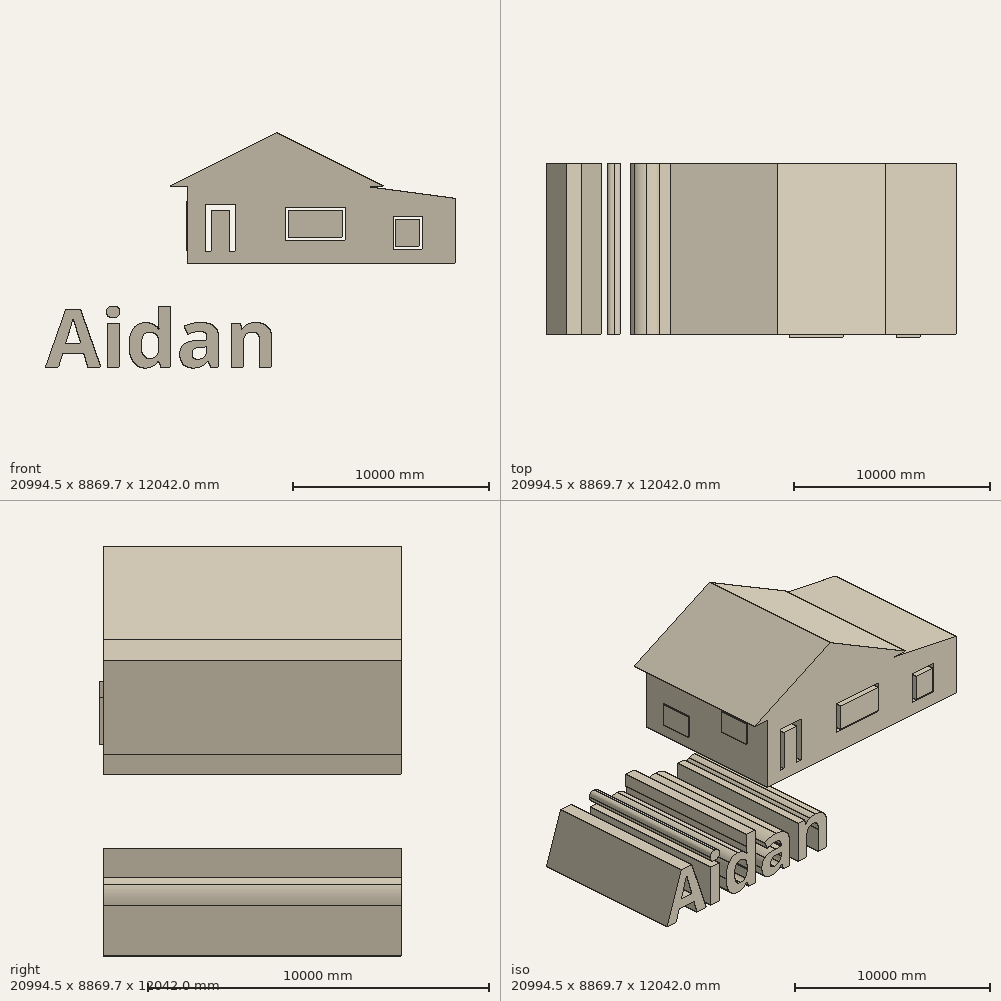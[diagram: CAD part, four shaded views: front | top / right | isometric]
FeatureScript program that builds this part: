
annotation { "Feature Type Name" : "Feature", "Feature Type Description" : "" }
export const myFeature = defineFeature(function(context is Context, id is Id, definition is map)
    precondition{}
    {
        {
            var Q0;
            Q0=qCreatedBy(makeId("Front.planeOp"),FACE);
            var sketch = newSketch(context, id + "F0", { "sketchPlane" : qUnion([Q0])});
            skLineSegment(sketch, "E0", {"start": v(0, 0) * mm, "end": v(-4572, 0) * mm});
            skLineSegment(sketch, "E1", {"start": v(0, 0) * mm, "end": v(4572, 0) * mm});
            skLineSegment(sketch, "E2", {"start": v(0, 0) * mm, "end": v(0, 2286) * mm});
            skLineSegment(sketch, "E3", {"start": v(0, 2286) * mm, "end": v(0, 2743.2) * mm});
            skLineSegment(sketch, "E4", {"start": v(0, 2286) * mm, "end": v(4572, 0) * mm});
            skLineSegment(sketch, "E5", {"start": v(0, 2286) * mm, "end": v(-4572, 0) * mm});
            skLineSegment(sketch, "E6", {"start": v(4572, 0) * mm, "end": v(5486.4, 0) * mm});
            skLineSegment(sketch, "E7", {"start": v(-4572, 0) * mm, "end": v(-5486.4, 0) * mm});
            skLineSegment(sketch, "E8", {"start": v(0, 2743.2) * mm, "end": v(-5486.4, 0) * mm});
            skLineSegment(sketch, "E9", {"start": v(0, 2743.2) * mm, "end": v(5486.4, 0) * mm});
            skLineSegment(sketch, "E10", {"start": v(-4572, 0) * mm, "end": v(-4572, -3352.8) * mm});
            skLineSegment(sketch, "E11", {"start": v(-4572, -3352.8) * mm, "end": v(4572, -3352.8) * mm});
            skLineSegment(sketch, "E12", {"start": v(4572, 0) * mm, "end": v(4572, -3352.8) * mm});
            skLineSegment(sketch, "E13", {"start": v(-4572, -3352.8) * mm, "end": v(-4572, -3962.4) * mm});
            skLineSegment(sketch, "E14.bottom", {"start": v(609.6, -1219.2) * mm, "end": v(3352.8, -1219.2) * mm});
            skLineSegment(sketch, "E14.top", {"start": v(609.6, -2590.8) * mm, "end": v(3352.8, -2590.8) * mm});
            skLineSegment(sketch, "E14.left", {"start": v(609.6, -1219.2) * mm, "end": v(609.6, -2590.8) * mm});
            skLineSegment(sketch, "E14.right", {"start": v(3352.8, -1219.2) * mm, "end": v(3352.8, -2590.8) * mm});
            skLineSegment(sketch, "E15", {"start": v(4572, -3352.8) * mm, "end": v(9144, -3352.8) * mm});
            skLineSegment(sketch, "E16.0", {"start": v(457.2, -1066.8) * mm, "end": v(3505.2, -1066.8) * mm});
            skLineSegment(sketch, "E16.1", {"start": v(457.2, -1066.8) * mm, "end": v(457.2, -2743.2) * mm});
            skLineSegment(sketch, "E16.2", {"start": v(457.2, -2743.2) * mm, "end": v(3505.2, -2743.2) * mm});
            skLineSegment(sketch, "E16.3", {"start": v(3505.2, -1066.8) * mm, "end": v(3505.2, -2743.2) * mm});
            skLineSegment(sketch, "E17", {"start": v(-3352.8, -3352.8) * mm, "end": v(-3352.8, -1219.2) * mm});
            skLineSegment(sketch, "E18", {"start": v(-3352.8, -1219.2) * mm, "end": v(-2438.4, -1219.2) * mm});
            skLineSegment(sketch, "E19", {"start": v(-2438.4, -1219.2) * mm, "end": v(-2438.4, -3352.8) * mm});
            skLineSegment(sketch, "E20.0", {"start": v(-2133.6, -914.4) * mm, "end": v(-2133.6, -3352.8) * mm});
            skLineSegment(sketch, "E20.1", {"start": v(-3657.6, -914.4) * mm, "end": v(-2133.6, -914.4) * mm});
            skLineSegment(sketch, "E20.2", {"start": v(-3657.6, -3352.8) * mm, "end": v(-3657.6, -914.4) * mm});
            skLineSegment(sketch, "E21", {"start": v(4572, 0) * mm, "end": v(9143.16, -609.6) * mm});
            skLineSegment(sketch, "E22", {"start": v(9143.16, -609.6) * mm, "end": v(9144, -3352.8) * mm});
            skLineSegment(sketch, "E23", {"start": v(4572, -922.5) * mm, "end": v(9144, -1532.2) * mm});
            skLineSegment(sketch, "E24.bottom", {"start": v(6096, -1697.6) * mm, "end": v(7315.2, -1697.6) * mm});
            skLineSegment(sketch, "E24.top", {"start": v(6096, -3069.2) * mm, "end": v(7315.2, -3069.2) * mm});
            skLineSegment(sketch, "E24.left", {"start": v(6096, -1697.6) * mm, "end": v(6096, -3069.2) * mm});
            skLineSegment(sketch, "E24.right", {"start": v(7315.2, -1697.6) * mm, "end": v(7315.2, -3069.2) * mm});
            skLineSegment(sketch, "E25.0", {"start": v(5943.6, -1545.2) * mm, "end": v(7467.6, -1545.2) * mm});
            skLineSegment(sketch, "E25.1", {"start": v(5943.6, -1545.2) * mm, "end": v(5943.6, -3221.6) * mm});
            skLineSegment(sketch, "E25.2", {"start": v(5943.6, -3221.6) * mm, "end": v(7467.6, -3221.6) * mm});
            skLineSegment(sketch, "E25.3", {"start": v(7467.6, -1545.2) * mm, "end": v(7467.6, -3221.6) * mm});
            skLineSegment(sketch, "E26", {"start": v(-4572, -3962.4) * mm, "end": v(4572, -3962.4) * mm});
            skLineSegment(sketch, "E27", {"start": v(4572, -3352.8) * mm, "end": v(4572, -3962.4) * mm});
            skLineSegment(sketch, "E28", {"start": v(9144, -3352.8) * mm, "end": v(9144, -3962.4) * mm});
            skLineSegment(sketch, "E29", {"start": v(9144, -3962.4) * mm, "end": v(4572, -3962.4) * mm});
            skText(sketch, "E30", { "text": "Aidan", "fontName": "OpenSans-Bold.ttf"});
            const initialGuessF0  = {"E30": [-11.85051, -9.25823, 1, 0, 2.96375]};
            skSetInitialGuess(sketch, initialGuessF0);
            skSolve(sketch);
        }
        {
            var Q0;
            Q0 = qSketchRegion(id + "F0", true);
            extrude(context, id + "F1", {"entities" : qUnion([Q0]), "depth" : 8747.76 * mm, "offsetDistance" : 30.48 * mm});
        }
        {
            var Q0;
            Q0=makeQuery(id+"F1.opExtrude","SWEPT_FACE",FACE,{"disambiguationData":[OSD([sQuery(id+"F0.wireOp",EDGE,"E10"),sQuery(id+"F0.wireOp",EDGE,"E13")])]});
            var sketch = newSketch(context, id + "F2", { "sketchPlane" : qUnion([Q0])});
            skLineSegment(sketch, "E31.bottom", {"start": v(1241.9, -2074) * mm, "end": v(3070.7, -2074) * mm});
            skLineSegment(sketch, "E31.top", {"start": v(1241.9, -3293.2) * mm, "end": v(3070.7, -3293.2) * mm});
            skLineSegment(sketch, "E31.left", {"start": v(1241.9, -2074) * mm, "end": v(1241.9, -3293.2) * mm});
            skLineSegment(sketch, "E31.right", {"start": v(3070.7, -2074) * mm, "end": v(3070.7, -3293.2) * mm});
            skPoint(sketch, "E32.oppositeSnap0", {"position": v(8747.76, -1981.2) * mm});
            skLineSegment(sketch, "E32.bottom", {"start": v(5471.72, -762) * mm, "end": v(7300.52, -762) * mm});
            skLineSegment(sketch, "E32.top", {"start": v(5471.72, -1981.2) * mm, "end": v(7300.52, -1981.2) * mm});
            skLineSegment(sketch, "E32.left", {"start": v(5471.72, -762) * mm, "end": v(5471.72, -1981.2) * mm});
            skLineSegment(sketch, "E32.right", {"start": v(7300.52, -762) * mm, "end": v(7300.52, -1981.2) * mm});
            skSolve(sketch);
        }
        {
            var Q0;
            Q0=makeQuery(id+"F2.imprint","IMPRINT",FACE,{"disambiguationData":[TD([[makeQuery(id+"F2.imprint","IMPRINT",EDGE,{"derivedFrom":sQuery(id+"F2.wireOp",EDGE,"E32.bottom")}),-1.0]])]});
            var Q1;
            Q1=makeQuery(id+"F2.imprint","IMPRINT",FACE,{"disambiguationData":[TD([[makeQuery(id+"F2.imprint","IMPRINT",EDGE,{"derivedFrom":sQuery(id+"F2.wireOp",EDGE,"E31.bottom")}),-1.0]])]});
            extrude(context, id + "F3", {"entities" : qUnion([Q0, Q1]), "operationType" : NewBodyOperationType.ADD, "depth" : 60.96 * mm, "offsetDistance" : 30.48 * mm});
        }
        {
            var Q0;
            {var subQ0=sQuery(id+"F0.wireOp",EDGE,"E17");Q0=makeQuery(id+"F0.imprint","IMPRINT",FACE,{"disambiguationData":[TD([[makeQuery(id+"F0.imprint","IMPRINT",EDGE,{"derivedFrom":subQ0}),-1.0]])]});}
            extrude(context, id + "F4", {"entities" : qUnion([Q0]), "operationType" : NewBodyOperationType.ADD, "depth" : 8747.76 * mm, "offsetDistance" : 30.48 * mm});
        }
        {
            var Q0;
            Q0=makeQuery(id+"F0.imprint","IMPRINT",FACE,{"disambiguationData":[TD([[makeQuery(id+"F0.imprint","IMPRINT",EDGE,{"derivedFrom":sQuery(id+"F0.wireOp",EDGE,"E14.bottom")}),-1.0]])]});
            var Q1;
            Q1=makeQuery(id+"F0.imprint","IMPRINT",FACE,{"disambiguationData":[TD([[makeQuery(id+"F0.imprint","IMPRINT",EDGE,{"derivedFrom":sQuery(id+"F0.wireOp",EDGE,"E24.bottom")}),-1.0]])]});
            extrude(context, id + "F5", {"entities" : qUnion([Q0, Q1]), "depth" : 30.48 * mm, "offsetDistance" : 30.48 * mm});
        }
        {
            var Q0;
            Q0=makeQuery(id+"F5.opExtrude","CAP_FACE",FACE,{"disambiguationData":[OSD([sQuery(id+"F0.wireOp",EDGE,"E14.bottom"),sQuery(id+"F0.wireOp",EDGE,"E14.top"),sQuery(id+"F0.wireOp",EDGE,"E14.left"),sQuery(id+"F0.wireOp",EDGE,"E14.right")])],"isStart":false});
            var Q1;
            Q1=makeQuery(id+"F5.opExtrude","CAP_FACE",FACE,{"disambiguationData":[OSD([sQuery(id+"F0.wireOp",EDGE,"E24.bottom"),sQuery(id+"F0.wireOp",EDGE,"E24.top"),sQuery(id+"F0.wireOp",EDGE,"E24.left"),sQuery(id+"F0.wireOp",EDGE,"E24.right")])],"isStart":false});
            extrude(context, id + "F6", {"entities" : qUnion([Q0, Q1]), "depth" : 8839.2 * mm, "offsetDistance" : 30.48 * mm});
        }
    });
